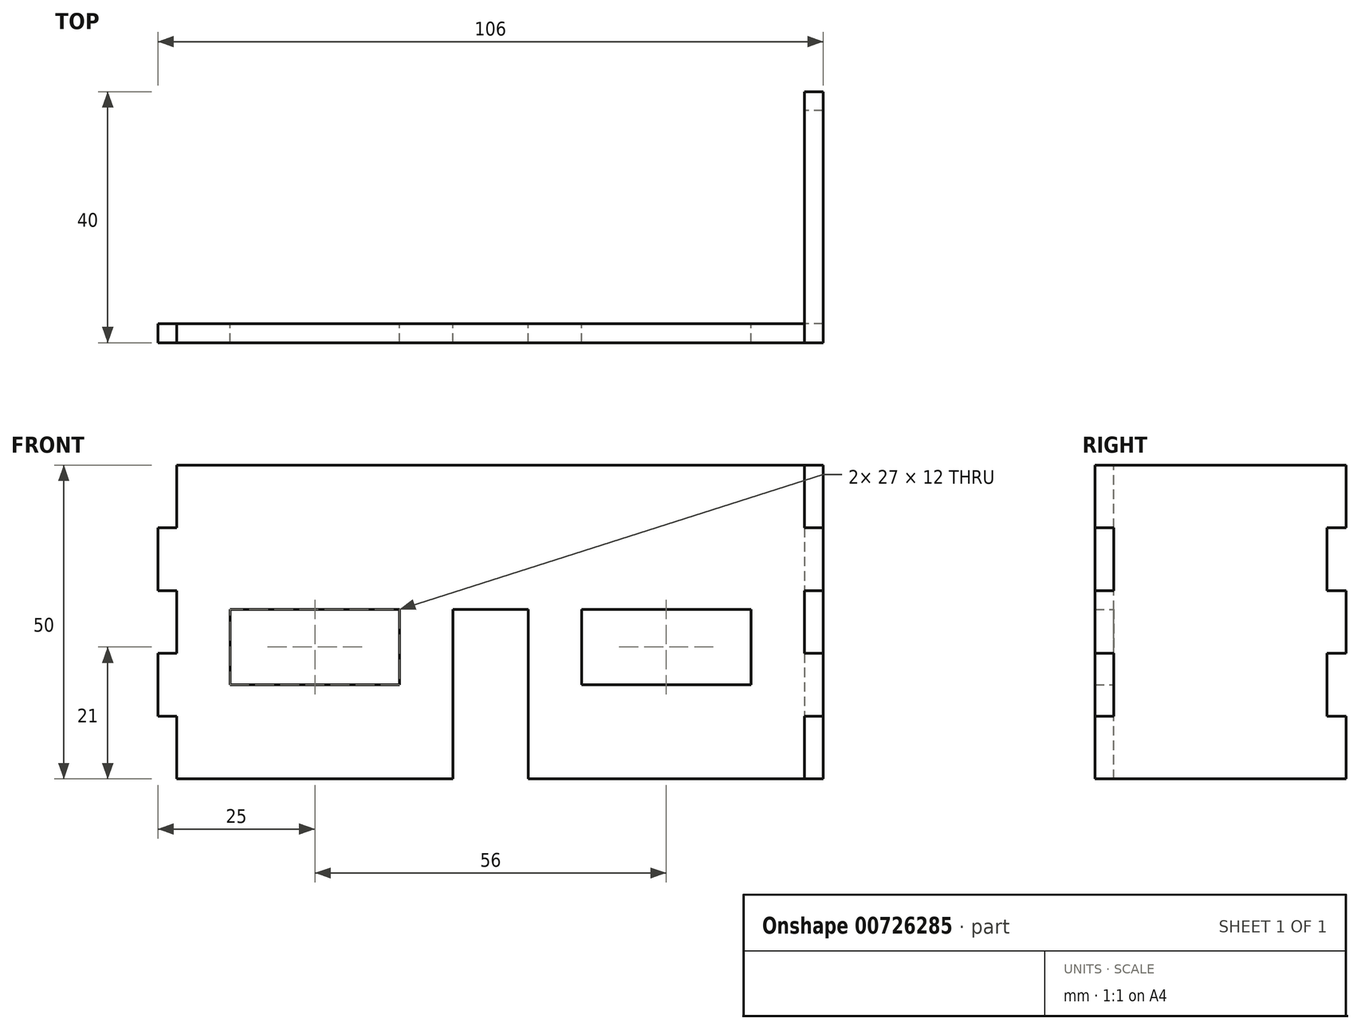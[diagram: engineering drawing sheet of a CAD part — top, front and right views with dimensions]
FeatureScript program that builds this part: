
annotation { "Feature Type Name" : "Feature", "Feature Type Description" : "" }
export const myFeature = defineFeature(function(context is Context, id is Id, definition is map)
    precondition{}
    {
        {
            var Q0;
            Q0=qCreatedBy(makeId("Front.planeOp"),FACE);
            var sketch = newSketch(context, id + "F0", { "sketchPlane" : qUnion([Q0])});
            skLineSegment(sketch, "E0.bottom", {"start": v(0, 0) * mm, "end": v(100, 0) * mm});
            skLineSegment(sketch, "E0.top", {"start": v(0, 50) * mm, "end": v(100, 50) * mm});
            skLineSegment(sketch, "E0.left", {"start": v(0, 0) * mm, "end": v(0, 10) * mm});
            skLineSegment(sketch, "E0.right", {"start": v(100, 0) * mm, "end": v(100, 10) * mm});
            skLineSegment(sketch, "E1", {"start": v(103, 40) * mm, "end": v(100, 40) * mm});
            skLineSegment(sketch, "E2", {"start": v(100, 40) * mm, "end": v(103, 40) * mm});
            skLineSegment(sketch, "E3", {"start": v(103, 30) * mm, "end": v(103, 40) * mm});
            skLineSegment(sketch, "E4", {"start": v(100, 30) * mm, "end": v(103, 30) * mm});
            skLineSegment(sketch, "E5", {"start": v(100, 20) * mm, "end": v(103, 20) * mm});
            skLineSegment(sketch, "E6", {"start": v(103, 20) * mm, "end": v(103, 10) * mm});
            skLineSegment(sketch, "E7", {"start": v(103, 10) * mm, "end": v(100, 10) * mm});
            skLineSegment(sketch, "E8.trimOffspring", {"start": v(100, 40) * mm, "end": v(100, 50) * mm});
            skLineSegment(sketch, "E9.trimOffspring", {"start": v(100, 20) * mm, "end": v(100, 30) * mm});
            skLineSegment(sketch, "E10", {"start": v(50, 50) * mm, "end": v(50, -35.06) * mm, "construction": true});
            skLineSegment(sketch, "E11.MirrorCS", {"start": v(-3, 30) * mm, "end": v(-3, 40) * mm});
            skLineSegment(sketch, "E12.MirrorCS", {"start": v(0, 40) * mm, "end": v(-3, 40) * mm});
            skLineSegment(sketch, "E13.MirrorCS", {"start": v(0, 20) * mm, "end": v(-3, 20) * mm});
            skLineSegment(sketch, "E14.MirrorCS", {"start": v(-3, 20) * mm, "end": v(-3, 10) * mm});
            skLineSegment(sketch, "E15.MirrorCS", {"start": v(-3, 10) * mm, "end": v(0, 10) * mm});
            skLineSegment(sketch, "E16.MirrorCS", {"start": v(0, 30) * mm, "end": v(-3, 30) * mm});
            skLineSegment(sketch, "E17.trimOffspring", {"start": v(0, 40) * mm, "end": v(0, 50) * mm});
            skLineSegment(sketch, "E18.trimOffspring", {"start": v(0, 20) * mm, "end": v(0, 30) * mm});
            skLineSegment(sketch, "E19.bottom", {"start": v(44, 0) * mm, "end": v(56, 0) * mm});
            skLineSegment(sketch, "E19.top", {"start": v(44, 27) * mm, "end": v(56, 27) * mm});
            skLineSegment(sketch, "E19.left", {"start": v(44, 0) * mm, "end": v(44, 27) * mm});
            skLineSegment(sketch, "E19.right", {"start": v(56, 0) * mm, "end": v(56, 27) * mm});
            skLineSegment(sketch, "E20.bottom", {"start": v(8.5, 27) * mm, "end": v(35.5, 27) * mm});
            skLineSegment(sketch, "E20.top", {"start": v(8.5, 15) * mm, "end": v(35.5, 15) * mm});
            skLineSegment(sketch, "E20.left", {"start": v(8.5, 27) * mm, "end": v(8.5, 15) * mm});
            skLineSegment(sketch, "E20.right", {"start": v(35.5, 27) * mm, "end": v(35.5, 15) * mm});
            skLineSegment(sketch, "E21.MirrorCS", {"start": v(91.5, 15) * mm, "end": v(64.5, 15) * mm});
            skLineSegment(sketch, "E22.MirrorCS", {"start": v(91.5, 27) * mm, "end": v(91.5, 15) * mm});
            skLineSegment(sketch, "E23.MirrorCS", {"start": v(91.5, 27) * mm, "end": v(64.5, 27) * mm});
            skLineSegment(sketch, "E24.MirrorCS", {"start": v(64.5, 27) * mm, "end": v(64.5, 15) * mm});
            skSolve(sketch);
        }
        {
            var Q0;
            Q0=makeQuery(id+"F0.imprint","IMPRINT",FACE,{"disambiguationData":[TD([[makeQuery(id+"F0.imprint","IMPRINT",EDGE,{"derivedFrom":sQuery(id+"F0.wireOp",EDGE,"E0.top")}),-1.0]])]});
            extrude(context, id + "F1", {"entities" : qUnion([Q0]), "depth" : 3 * mm, "offsetDistance" : 25 * mm});
        }
        {
            var Q0;
            Q0=makeQuery(id+"F1.opExtrude","SWEPT_FACE",FACE,{"disambiguationData":[OSD([sQuery(id+"F0.wireOp",EDGE,"E9.trimOffspring")])]});
            var sketch = newSketch(context, id + "F2", { "sketchPlane" : qUnion([Q0])});
            skLineSegment(sketch, "E25", {"start": v(-3, 50) * mm, "end": v(-3, 40) * mm});
            skLineSegment(sketch, "E26", {"start": v(-3, 40) * mm, "end": v(0, 40) * mm});
            skLineSegment(sketch, "E27", {"start": v(0, 40) * mm, "end": v(0, 30) * mm});
            skLineSegment(sketch, "E28", {"start": v(0, 30) * mm, "end": v(-3, 30) * mm});
            skLineSegment(sketch, "E29", {"start": v(-3, 30) * mm, "end": v(-3, 20) * mm});
            skLineSegment(sketch, "E30", {"start": v(-3, 20) * mm, "end": v(0, 20) * mm});
            skLineSegment(sketch, "E31", {"start": v(0, 20) * mm, "end": v(0, 10) * mm});
            skLineSegment(sketch, "E32", {"start": v(0, 10) * mm, "end": v(-3, 10) * mm});
            skLineSegment(sketch, "E33", {"start": v(-3, 10) * mm, "end": v(-3, 0) * mm});
            skLineSegment(sketch, "E34", {"start": v(-3, 0) * mm, "end": v(37, 0) * mm});
            skLineSegment(sketch, "E35", {"start": v(37, 50) * mm, "end": v(-3, 50) * mm});
            skLineSegment(sketch, "E36", {"start": v(17, 50) * mm, "end": v(17, -5.3) * mm, "construction": true});
            skLineSegment(sketch, "E37.MirrorCS", {"start": v(37, 50) * mm, "end": v(37, 40) * mm});
            skLineSegment(sketch, "E38.MirrorCS", {"start": v(37, 30) * mm, "end": v(37, 20) * mm});
            skLineSegment(sketch, "E39.MirrorCS", {"start": v(34, 30) * mm, "end": v(37, 30) * mm});
            skLineSegment(sketch, "E40.MirrorCS", {"start": v(37, 10) * mm, "end": v(37, 0) * mm});
            skLineSegment(sketch, "E41.MirrorCS", {"start": v(34, 40) * mm, "end": v(34, 30) * mm});
            skLineSegment(sketch, "E42.MirrorCS", {"start": v(34, 20) * mm, "end": v(34, 10) * mm});
            skLineSegment(sketch, "E43.MirrorCS", {"start": v(34, 10) * mm, "end": v(37, 10) * mm});
            skLineSegment(sketch, "E44.MirrorCS", {"start": v(37, 40) * mm, "end": v(34, 40) * mm});
            skLineSegment(sketch, "E45.MirrorCS", {"start": v(37, 20) * mm, "end": v(34, 20) * mm});
            skSolve(sketch);
        }
        {
            var Q0;
            Q0 = qSketchRegion(id + "F2", true);
            extrude(context, id + "F3", {"entities" : qUnion([Q0]), "depth" : 3 * mm, "offsetDistance" : 25 * mm});
        }
    });
